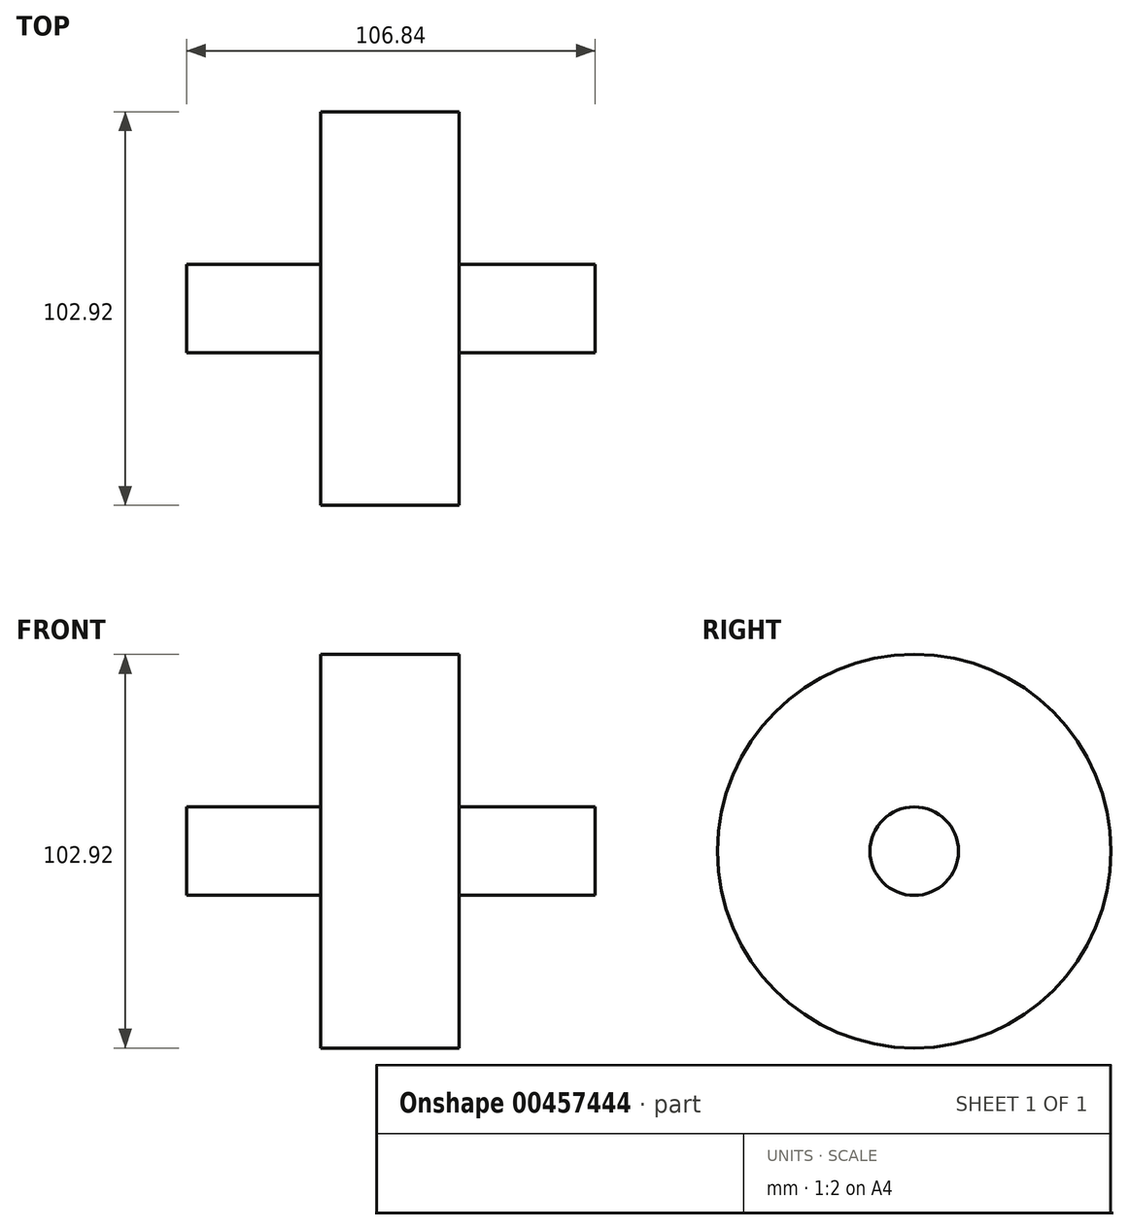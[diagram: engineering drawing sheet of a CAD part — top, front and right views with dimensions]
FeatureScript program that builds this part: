
annotation { "Feature Type Name" : "Feature", "Feature Type Description" : "" }
export const myFeature = defineFeature(function(context is Context, id is Id, definition is map)
    precondition{}
    {
        {
            var Q0;
            Q0=qCreatedBy(makeId("Front.planeOp"),FACE);
            var sketch = newSketch(context, id + "F0", { "sketchPlane" : qUnion([Q0])});
            skLineSegment(sketch, "E0", {"start": v(-133.25, 0) * mm, "end": v(116.09, 0) * mm});
            skLineSegment(sketch, "E1", {"start": v(0, 0) * mm, "end": v(0, 11.56) * mm});
            skLineSegment(sketch, "E2", {"start": v(0, 11.56) * mm, "end": v(35.14, 11.56) * mm});
            skLineSegment(sketch, "E3", {"start": v(35.14, 11.56) * mm, "end": v(35.14, 51.46) * mm});
            skLineSegment(sketch, "E4", {"start": v(35.14, 51.46) * mm, "end": v(71.28, 51.46) * mm});
            skLineSegment(sketch, "E5", {"start": v(71.28, 51.46) * mm, "end": v(71.28, 11.56) * mm});
            skLineSegment(sketch, "E6", {"start": v(71.28, 11.56) * mm, "end": v(106.84, 11.56) * mm});
            skLineSegment(sketch, "E7", {"start": v(106.84, 11.56) * mm, "end": v(106.84, 0) * mm});
            skSolve(sketch);
        }
        {
            var Q0;
            Q0 = qSketchRegion(id + "F0", true);
            var Q1;
            Q1=sQuery(id+"F0.wireOp",EDGE,"E0");
            revolve(context, id + "F1", {"entities" : qUnion([Q0]), "axis" : qUnion([Q1]), "revolveType" : RevolveType.FULL});
        }
    });
